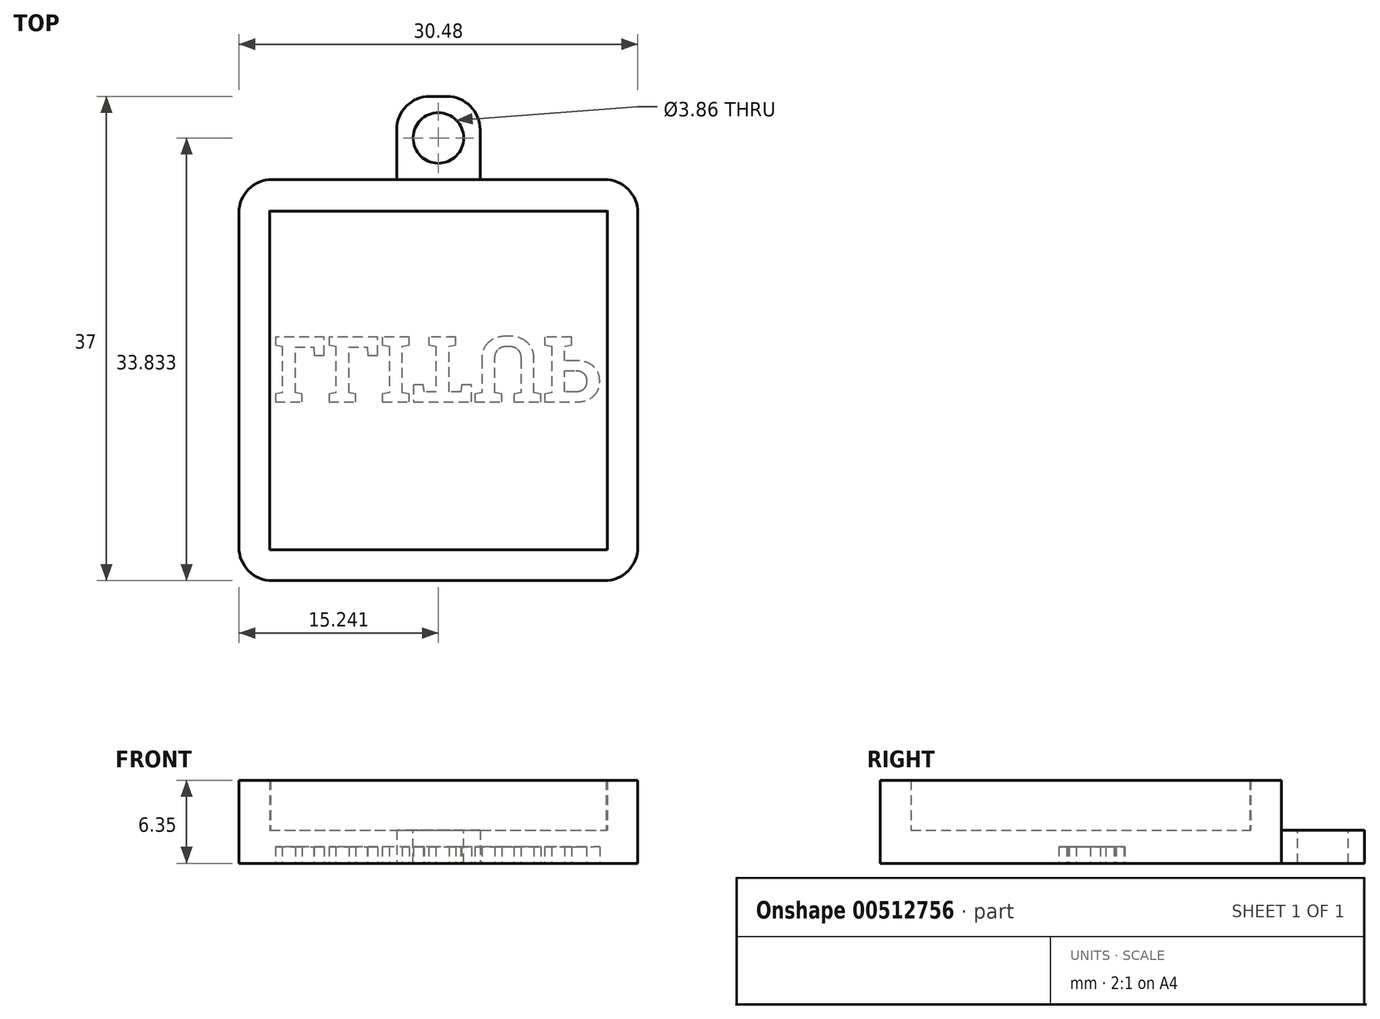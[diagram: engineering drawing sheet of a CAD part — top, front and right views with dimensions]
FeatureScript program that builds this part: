
annotation { "Feature Type Name" : "Feature", "Feature Type Description" : "" }
export const myFeature = defineFeature(function(context is Context, id is Id, definition is map)
    precondition{}
    {
        {
            var Q0;
            Q0=qCreatedBy(makeId("Top.planeOp"),FACE);
            var sketch = newSketch(context, id + "F0", { "sketchPlane" : qUnion([Q0])});
            skLineSegment(sketch, "E0.bottom", {"start": v(15.24, -15.33) * mm, "end": v(-15.24, -15.33) * mm});
            skLineSegment(sketch, "E0.top", {"start": v(15.24, 15.33) * mm, "end": v(3.2, 15.33) * mm});
            skLineSegment(sketch, "E0.left", {"start": v(15.24, -15.33) * mm, "end": v(15.24, 15.33) * mm});
            skLineSegment(sketch, "E0.right", {"start": v(-15.24, -15.33) * mm, "end": v(-15.24, 15.33) * mm});
            skPoint(sketch, "E0.middle", {"position": v(0, 0) * mm});
            skLineSegment(sketch, "E1", {"start": v(0, -15.33) * mm, "end": v(0, 0) * mm});
            skLineSegment(sketch, "E2", {"start": v(0, -15.33) * mm, "end": v(0, 35.12) * mm});
            skLineSegment(sketch, "E3.left", {"start": v(3.2, 15.33) * mm, "end": v(3.2, 16.84) * mm});
            skPoint(sketch, "E3.middle", {"position": v(0, 15.33) * mm});
            skPoint(sketch, "E4.orphan", {"position": v(3.2, 13.82) * mm});
            skPoint(sketch, "E5.orphan", {"position": v(-3.2, 13.82) * mm});
            skLineSegment(sketch, "E6.top", {"start": v(3.2, 21.67) * mm, "end": v(-3.2, 21.67) * mm});
            skLineSegment(sketch, "E6.left", {"start": v(3.2, 16.84) * mm, "end": v(3.2, 21.67) * mm});
            skLineSegment(sketch, "E6.right", {"start": v(-3.2, 15.33) * mm, "end": v(-3.2, 21.67) * mm});
            skPoint(sketch, "E3.right.end.orphan", {"position": v(-3.2, 16.84) * mm});
            skLineSegment(sketch, "E7.trimOffspring", {"start": v(-3.2, 15.33) * mm, "end": v(-15.24, 15.33) * mm});
            skSolve(sketch);
        }
        {
            var Q0;
            Q0 = qSketchRegion(id + "F0", true);
            extrude(context, id + "F1", {"entities" : qUnion([Q0]), "depth" : 2.54 * mm});
        }
        {
            var Q0;
            Q0=makeQuery(id+"F1.opExtrude","CAP_FACE",FACE,{"disambiguationData":[OSD([sQuery(id+"F0.wireOp",EDGE,"E0.bottom"),sQuery(id+"F0.wireOp",EDGE,"E0.top"),sQuery(id+"F0.wireOp",EDGE,"E0.left"),sQuery(id+"F0.wireOp",EDGE,"E0.right"),sQuery(id+"F0.wireOp",EDGE,"E3.left"),sQuery(id+"F0.wireOp",EDGE,"E6.top"),sQuery(id+"F0.wireOp",EDGE,"E6.left"),sQuery(id+"F0.wireOp",EDGE,"E6.right"),sQuery(id+"F0.wireOp",EDGE,"E7.trimOffspring")])],"isStart":false});
            var sketch = newSketch(context, id + "F2", { "sketchPlane" : qUnion([Q0])});
            skLineSegment(sketch, "E8", {"start": v(-12.9, 12.98) * mm, "end": v(-12.83, 12.9) * mm});
            skLineSegment(sketch, "E9", {"start": v(12.9, 12.98) * mm, "end": v(12.83, 12.9) * mm});
            skLineSegment(sketch, "E10", {"start": v(-12.9, -12.98) * mm, "end": v(-12.9, 12.98) * mm});
            skLineSegment(sketch, "E11", {"start": v(12.9, -12.98) * mm, "end": v(12.9, 12.98) * mm});
            skLineSegment(sketch, "E12", {"start": v(-12.9, 12.9) * mm, "end": v(12.9, 12.9) * mm});
            skLineSegment(sketch, "E13", {"start": v(-12.9, -12.98) * mm, "end": v(12.9, -12.98) * mm});
            skLineSegment(sketch, "E14.bottom", {"start": v(-15.24, 15.33) * mm, "end": v(15.24, 15.33) * mm});
            skLineSegment(sketch, "E14.top", {"start": v(-15.24, -15.33) * mm, "end": v(15.24, -15.33) * mm});
            skLineSegment(sketch, "E14.left", {"start": v(-15.24, 15.33) * mm, "end": v(-15.24, -15.33) * mm});
            skLineSegment(sketch, "E14.right", {"start": v(15.24, 15.33) * mm, "end": v(15.24, -15.33) * mm});
            skSolve(sketch);
        }
        {
            var Q0;
            {var subQ5=sQuery(id+"F2.wireOp",EDGE,"E8");Q0=makeQuery(id+"F2.imprint","IMPRINT",FACE,{"disambiguationData":[TD([[makeQuery(id+"F2.imprint","IMPRINT",EDGE,{"derivedFrom":subQ5}),1.0]])]});}
            extrude(context, id + "F3", {"entities" : qUnion([Q0]), "operationType" : NewBodyOperationType.ADD, "depth" : 3.8 * mm});
        }
        {
            var Q0;
            {var subQ0=sQuery(id+"F0.wireOp",EDGE,"E6.top");var subQ1=sQuery(id+"F0.wireOp",EDGE,"E6.left");var subQ2=sQuery(id+"F0.wireOp",EDGE,"E3.left");var subQ3=sQuery(id+"F0.wireOp",EDGE,"E6.right");var subQ4=sQuery(id+"F0.wireOp",EDGE,"E0.top");var subQ5=sQuery(id+"F0.wireOp",EDGE,"E7.trimOffspring");Q0=makeQuery(id+"F3.boolean.opBoolean","SPLIT",FACE,{"disambiguationData":[TD([makeQuery(id+"F1.opExtrude","SWEPT_FACE",FACE,{"disambiguationData":[OSD([subQ4])]})])],"derivedFrom":makeQuery(id+"F1.opExtrude","CAP_FACE",FACE,{"disambiguationData":[OSD([sQuery(id+"F0.wireOp",EDGE,"E0.bottom"),subQ4,sQuery(id+"F0.wireOp",EDGE,"E0.left"),sQuery(id+"F0.wireOp",EDGE,"E0.right"),subQ2,subQ0,subQ1,subQ3,subQ5])],"isStart":false})});}
            var sketch = newSketch(context, id + "F4", { "sketchPlane" : qUnion([Q0])});
            skLineSegment(sketch, "E15", {"start": v(-3.2, 15.33) * mm, "end": v(3.2, 21.67) * mm});
            skLineSegment(sketch, "E16", {"start": v(3.2, 15.33) * mm, "end": v(-3.2, 21.67) * mm});
            skPoint(sketch, "E17", {"position": v(0, 18.5) * mm});
            skCircle(sketch, "E18", {"center": v(0, 18.5) * mm, "radius": 1.92 * mm});
            skSolve(sketch);
        }
        {
            var Q0;
            Q0=sQuery(id+"F4.wireOp",VERTEX,"E17");
            var Q1;
            Q1=makeQuery(id+"F1.opExtrude","SWEPT_BODY",BODY,{"disambiguationData":[OSD([sQuery(id+"F0.wireOp",EDGE,"E0.bottom"),sQuery(id+"F0.wireOp",EDGE,"E0.top"),sQuery(id+"F0.wireOp",EDGE,"E0.left"),sQuery(id+"F0.wireOp",EDGE,"E0.right"),sQuery(id+"F0.wireOp",EDGE,"E3.left"),sQuery(id+"F0.wireOp",EDGE,"E6.top"),sQuery(id+"F0.wireOp",EDGE,"E6.left"),sQuery(id+"F0.wireOp",EDGE,"E6.right"),sQuery(id+"F0.wireOp",EDGE,"E7.trimOffspring")])]});
            hole(context, id + "F5", {"style" : HoleStyle.SIMPLE, "endStyle" : HoleEndStyle.BLIND, "holeDiameter" : 3.86 * mm, "holeDepth" : 12.7 * mm, "isTappedThrough" : true, "tappedDepth" : 12.7 * mm, "tapClearance" : 3, "locations" : qUnion([Q0]), "scope" : qUnion([Q1])});
        }
        {
            var Q0;
            Q0=makeQuery(id+"F3.boolean.opBoolean","MERGE",EDGE,{"derivedFrom":[makeQuery(id+"F1.opExtrude","SWEPT_EDGE",EDGE,{"disambiguationData":[OSD([sQuery(id+"F0.wireOp",EDGE,"E0.right"),sQuery(id+"F0.wireOp",EDGE,"E7.trimOffspring")])]}),makeQuery(id+"F3.opExtrude","SWEPT_EDGE",EDGE,{"disambiguationData":[OSD([sQuery(id+"F2.wireOp",EDGE,"E14.bottom"),sQuery(id+"F2.wireOp",EDGE,"E14.left")])]})]});
            fillet(context, id + "F6", {"entities" : qUnion([Q0]), "radius" : 2.54 * mm, "tangentPropagation" : true, "allowEdgeOverflow" : false});
        }
        {
            var Q0;
            Q0=makeQuery(id+"F3.boolean.opBoolean","MERGE",EDGE,{"derivedFrom":[makeQuery(id+"F1.opExtrude","SWEPT_EDGE",EDGE,{"disambiguationData":[OSD([sQuery(id+"F0.wireOp",EDGE,"E0.bottom"),sQuery(id+"F0.wireOp",EDGE,"E0.right")])]}),makeQuery(id+"F3.opExtrude","SWEPT_EDGE",EDGE,{"disambiguationData":[OSD([sQuery(id+"F2.wireOp",EDGE,"E14.top"),sQuery(id+"F2.wireOp",EDGE,"E14.left")])]})]});
            var Q1;
            Q1=makeQuery(id+"F3.boolean.opBoolean","MERGE",EDGE,{"derivedFrom":[makeQuery(id+"F1.opExtrude","SWEPT_EDGE",EDGE,{"disambiguationData":[OSD([sQuery(id+"F0.wireOp",EDGE,"E0.bottom"),sQuery(id+"F0.wireOp",EDGE,"E0.left")])]}),makeQuery(id+"F3.opExtrude","SWEPT_EDGE",EDGE,{"disambiguationData":[OSD([sQuery(id+"F2.wireOp",EDGE,"E14.top"),sQuery(id+"F2.wireOp",EDGE,"E14.right")])]})]});
            var Q2;
            Q2=makeQuery(id+"F3.boolean.opBoolean","MERGE",EDGE,{"derivedFrom":[makeQuery(id+"F1.opExtrude","SWEPT_EDGE",EDGE,{"disambiguationData":[OSD([sQuery(id+"F0.wireOp",EDGE,"E0.top"),sQuery(id+"F0.wireOp",EDGE,"E0.left")])]}),makeQuery(id+"F3.opExtrude","SWEPT_EDGE",EDGE,{"disambiguationData":[OSD([sQuery(id+"F2.wireOp",EDGE,"E14.bottom"),sQuery(id+"F2.wireOp",EDGE,"E14.right")])]})]});
            var Q3;
            Q3=makeQuery(id+"F1.opExtrude","SWEPT_EDGE",EDGE,{"disambiguationData":[OSD([sQuery(id+"F0.wireOp",EDGE,"E6.top"),sQuery(id+"F0.wireOp",EDGE,"E6.left")])]});
            var Q4;
            Q4=makeQuery(id+"F1.opExtrude","SWEPT_EDGE",EDGE,{"disambiguationData":[OSD([sQuery(id+"F0.wireOp",EDGE,"E6.top"),sQuery(id+"F0.wireOp",EDGE,"E6.right")])]});
            fillet(context, id + "F7", {"entities" : qUnion([Q0, Q1, Q2, Q3, Q4]), "radius" : 2.54 * mm, "tangentPropagation" : true, "allowEdgeOverflow" : false});
        }
        {
            var Q0;
            Q0=makeQuery(id+"F1.opExtrude","CAP_FACE",FACE,{"disambiguationData":[OSD([sQuery(id+"F0.wireOp",EDGE,"E0.bottom"),sQuery(id+"F0.wireOp",EDGE,"E0.top"),sQuery(id+"F0.wireOp",EDGE,"E0.left"),sQuery(id+"F0.wireOp",EDGE,"E0.right"),sQuery(id+"F0.wireOp",EDGE,"E3.left"),sQuery(id+"F0.wireOp",EDGE,"E6.top"),sQuery(id+"F0.wireOp",EDGE,"E6.left"),sQuery(id+"F0.wireOp",EDGE,"E6.right"),sQuery(id+"F0.wireOp",EDGE,"E7.trimOffspring")])],"isStart":true});
            var sketch = newSketch(context, id + "F8", { "sketchPlane" : qUnion([Q0])});
            skText(sketch, "E19", { "text": "LLITUP", "fontName": "RobotoSlab-Bold.ttf"});
            const initialGuessF8  = {"E19": [-0.01265, -0.00329, 1, 0, 0.00503]};
            skSetInitialGuess(sketch, initialGuessF8);
            skSolve(sketch);
        }
        {
            var Q0;
            Q0 = qSketchRegion(id + "F8", true);
            extrude(context, id + "F9", {"entities" : qUnion([Q0]), "operationType" : NewBodyOperationType.REMOVE, "oppositeDirection" : true, "depth" : 1.27 * mm, "offsetDistance" : 25.4 * mm});
        }
    });
